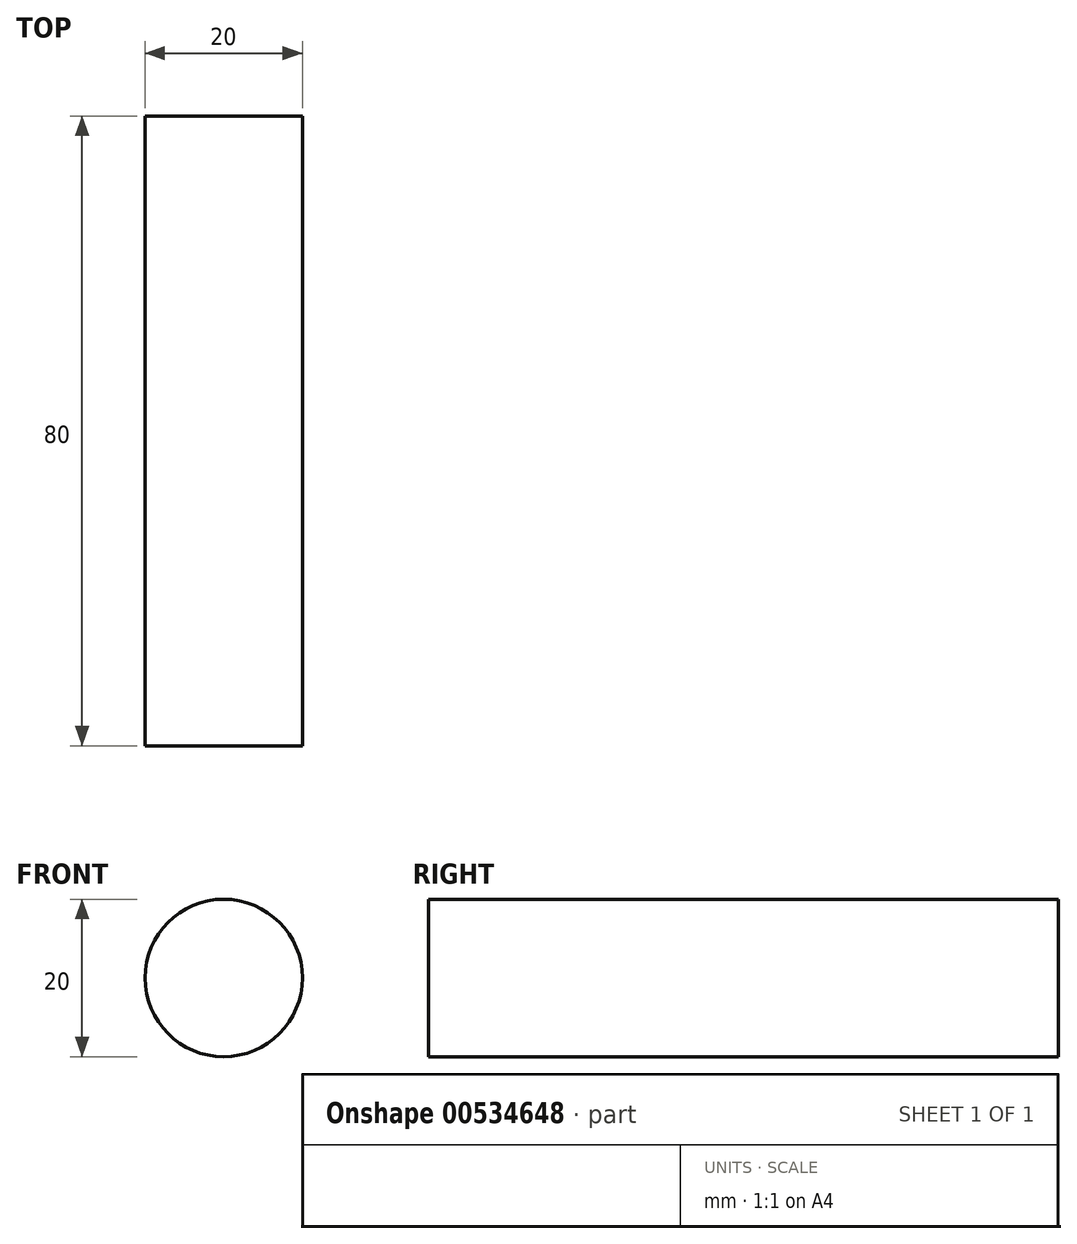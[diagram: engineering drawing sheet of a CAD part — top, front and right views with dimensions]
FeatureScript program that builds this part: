
annotation { "Feature Type Name" : "Feature", "Feature Type Description" : "" }
export const myFeature = defineFeature(function(context is Context, id is Id, definition is map)
    precondition{}
    {
        {
            var Q0;
            Q0=qCreatedBy(makeId("Front.planeOp"),FACE);
            var sketch = newSketch(context, id + "F0", { "sketchPlane" : qUnion([Q0])});
            skCircle(sketch, "E0", {"center": v(0, 0) * mm, "radius": 10 * mm});
            skSolve(sketch);
        }
        {
            var Q0;
            Q0=qSketchRegion(id+"F0",true);
            extrude(context, id + "F1", {"entities" : qUnion([Q0]), "depth" : 80 * mm, "offsetDistance" : 25 * mm});
        }
    });
